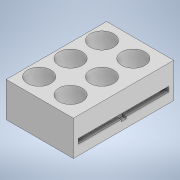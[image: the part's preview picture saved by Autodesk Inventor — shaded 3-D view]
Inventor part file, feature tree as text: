
AUTODESK INVENTOR PART (.ipt)
format: ipt  version: 2020 (Build 240168000, 168)  size: 262,656 bytes
history: native  units: in
note: dims shown in document units (in); Inventor stores cm internally (conversion verified against a paired STEP export)
features: extrude x7, sketch x7, pattern_linear x1
ambient origin geometry x8: Origin, YZ Plane, XZ Plane, XY Plane, X Axis, Y Axis, Z Axis, Center Point
bodies: Solid1 (feature_tree)
feature tree (15):
  extrude  "Extrusion1"  Depth=5.0299in
  extrude  "Extrusion2"  Depth=0.375in
  extrude  "Extrusion3"  Depth=0.5in
  sketch  "Sketch5"  dims[d24=5.315in d25=4.5472in]
  extrude  "Extrusion16"  Depth=4.5472in
  extrude  "Extrusion17"  Depth=0.25in
  extrude  "Extrusion18"  Depth=0.1in
  pattern_linear  "Rectangular Pattern2"  Spacing1=1.25in  [1 undecoded]
  extrude  "Extrusion19"  Depth=0.25in TaperAngle=0.0deg
  sketch  "Sketch1"  dims[d0=3.3654in d1=5.0299in]
  sketch  "Sketch3"  dims[d3=45.0deg d4=0.375in]
  sketch  "Sketch4"  dims[d5=0.5in d6=0.0in d23=2.8543in]
  sketch  "Sketch22"  dims[d26=0.1in d27=0.0in d28=0.25in]
  sketch  "Sketch23"  dims[d29=0.1in d30=0.0in d31=2.6575in]
  sketch  "Sketch24"  dims[d32=1.05in d33=1.25in d154=0.25in d155=0.0in d156=1.0in d157=0.0in d158=1.1787in d159=1.5in d160=0.0in d161=1.1811in d163=1.5748in d164=0.7874in d166=1.5748in d167=0.5in d168=1.5in d169=0.0in d45=1.0in d46=1.0in d47=1.0in d48=0.15in d49=0.201in d50=0.375in d51=0.5635in d52=0.75in d53=0.8108in d54=0.0625in d55=0.75in d56=0.375in]
note: 1 required parameter value undecoded (feature->parameter linkage not recoverable at this tier; creation-order binding heuristic only, values carry confidence <= 0.55)
